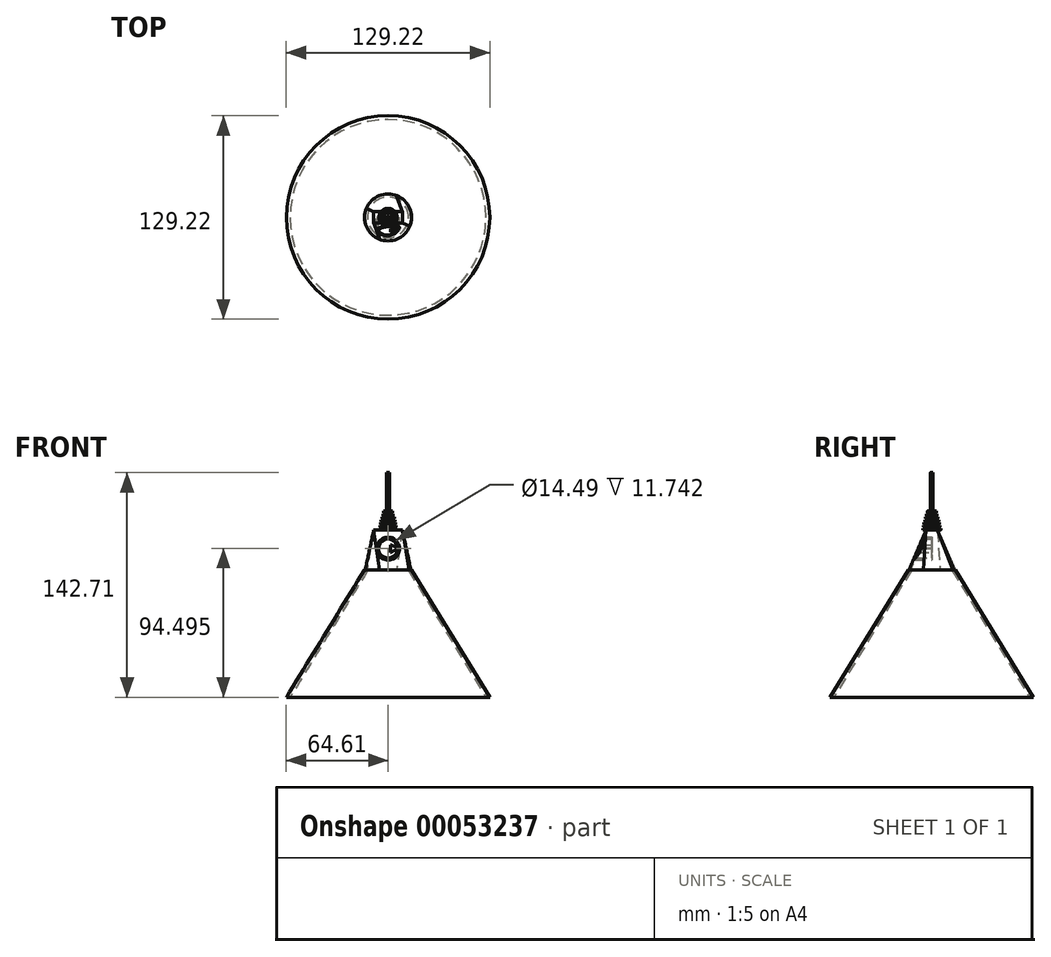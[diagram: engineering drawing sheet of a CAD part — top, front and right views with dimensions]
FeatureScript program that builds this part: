
annotation { "Feature Type Name" : "Feature", "Feature Type Description" : "" }
export const myFeature = defineFeature(function(context is Context, id is Id, definition is map)
    precondition{}
    {
        {
            var Q0;
            Q0=qCreatedBy(makeId("Top.planeOp"),FACE);
            var sketch = newSketch(context, id + "F0", { "sketchPlane" : qUnion([Q0])});
            skLineSegment(sketch, "E0.bottom", {"start": v(-9.08, 3.6) * mm, "end": v(9.08, 3.6) * mm});
            skLineSegment(sketch, "E0.top", {"start": v(-9.08, -3.6) * mm, "end": v(9.08, -3.6) * mm});
            skLineSegment(sketch, "E0.left", {"start": v(-9.08, 3.6) * mm, "end": v(-9.08, -3.6) * mm});
            skLineSegment(sketch, "E0.right", {"start": v(9.08, 3.6) * mm, "end": v(9.08, -3.6) * mm});
            skLineSegment(sketch, "E1", {"start": v(0, 3.6) * mm, "end": v(0, -3.6) * mm, "construction": true});
            skLineSegment(sketch, "E2", {"start": v(-9.08, 0) * mm, "end": v(9.08, 0) * mm, "construction": true});
            skSolve(sketch);
        }
        {
            var Q0;
            Q0=qCreatedBy(makeId("Top.planeOp"),FACE);
            cPlane(context, id + "F1", {"entities" : qUnion([Q0]), "cplaneType" : CPlaneType.OFFSET, "offset" : 25.4 * mm, "oppositeDirection" : true, "width" : 152.4 * mm, "height" : 152.4 * mm});
        }
        {
            var Q0;
            Q0=qCreatedBy(id+"F1.planeOp",FACE);
            var sketch = newSketch(context, id + "F2", { "sketchPlane" : qUnion([Q0])});
            skCircle(sketch, "E3", {"center": v(0, 0) * mm, "radius": 14.52 * mm});
            skSolve(sketch);
        }
        {
            var Q0;
            Q0=makeQuery(id+"F0.imprint","IMPRINT",FACE,{"disambiguationData":[TD([[makeQuery(id+"F0.imprint","IMPRINT",EDGE,{"derivedFrom":sQuery(id+"F0.wireOp",EDGE,"E0.bottom")}),-1.0]])]});
            var Q1;
            Q1=makeQuery(id+"F2.imprint","IMPRINT",FACE,{"disambiguationData":[TD([[makeQuery(id+"F2.imprint","IMPRINT",EDGE,{"derivedFrom":sQuery(id+"F2.wireOp",EDGE,"E3")}),1.0]])]});
            loft(context, id + "F3", {"sheetProfilesArray" : [{ "sheetProfileEntities" : qUnion([Q0]) }, { "sheetProfileEntities" : qUnion([Q1]) }]});
        }
        {
            var Q0;
            Q0=qCreatedBy(makeId("Front.planeOp"),FACE);
            var sketch = newSketch(context, id + "F4", { "sketchPlane" : qUnion([Q0])});
            skLineSegment(sketch, "E4", {"start": v(-14.94, -25.3) * mm, "end": v(-64.6, -106.22) * mm});
            skLineSegment(sketch, "E5", {"start": v(-64.6, -106.22) * mm, "end": v(-62.17, -106.22) * mm});
            skLineSegment(sketch, "E6", {"start": v(-62.17, -106.22) * mm, "end": v(-12.95, -25.52) * mm});
            skLineSegment(sketch, "E7", {"start": v(-12.95, -25.52) * mm, "end": v(-14.94, -25.3) * mm});
            skLineSegment(sketch, "E8", {"start": v(0, -122.63) * mm, "end": v(0, -14.43) * mm, "construction": true});
            skSolve(sketch);
        }
        {
            var Q0;
            Q0 = qSketchRegion(id + "F4", true);
            var Q1;
            Q1=sQuery(id+"F4.wireOp",EDGE,"E8");
            revolve(context, id + "F5", {"entities" : qUnion([Q0]), "axis" : qUnion([Q1]), "revolveType" : RevolveType.FULL});
        }
        {
            var Q0;
            Q0=qCreatedBy(makeId("Front.planeOp"),FACE);
            var sketch = newSketch(context, id + "F6", { "sketchPlane" : qUnion([Q0])});
            skLineSegment(sketch, "E9", {"start": v(0, 36.49) * mm, "end": v(0.88, 36.49) * mm});
            skLineSegment(sketch, "E10", {"start": v(0.88, 36.49) * mm, "end": v(0.88, 11.98) * mm});
            skLineSegment(sketch, "E11", {"start": v(0.88, 11.98) * mm, "end": v(2.84, 11.98) * mm});
            skLineSegment(sketch, "E12", {"start": v(2.84, 11.98) * mm, "end": v(2.84, 10.89) * mm});
            skLineSegment(sketch, "E13", {"start": v(2.84, 10.89) * mm, "end": v(0.88, 10.89) * mm});
            skLineSegment(sketch, "E14", {"start": v(0.88, 10.89) * mm, "end": v(0.88, 10.17) * mm});
            skLineSegment(sketch, "E15", {"start": v(0.88, 10.17) * mm, "end": v(3.29, 10.17) * mm});
            skLineSegment(sketch, "E16", {"start": v(3.29, 10.17) * mm, "end": v(3.29, 9.07) * mm});
            skLineSegment(sketch, "E17", {"start": v(3.29, 9.07) * mm, "end": v(0.88, 9.07) * mm});
            skLineSegment(sketch, "E18", {"start": v(0.88, 9.07) * mm, "end": v(0.88, 8.35) * mm});
            skLineSegment(sketch, "E19", {"start": v(0.88, 8.35) * mm, "end": v(3.96, 8.35) * mm});
            skLineSegment(sketch, "E20", {"start": v(3.96, 8.35) * mm, "end": v(3.96, 7.26) * mm});
            skLineSegment(sketch, "E21", {"start": v(3.96, 7.26) * mm, "end": v(0.88, 7.26) * mm});
            skLineSegment(sketch, "E22", {"start": v(0.88, 7.26) * mm, "end": v(0.88, 6.54) * mm});
            skLineSegment(sketch, "E23", {"start": v(0.88, 6.54) * mm, "end": v(4.5, 6.54) * mm});
            skLineSegment(sketch, "E24", {"start": v(4.5, 6.54) * mm, "end": v(4.5, 5.44) * mm});
            skLineSegment(sketch, "E25", {"start": v(4.5, 5.44) * mm, "end": v(0.88, 5.44) * mm});
            skLineSegment(sketch, "E26", {"start": v(0.88, 5.44) * mm, "end": v(0.88, 4.72) * mm});
            skLineSegment(sketch, "E27", {"start": v(0.88, 4.72) * mm, "end": v(4.88, 4.72) * mm});
            skLineSegment(sketch, "E28", {"start": v(4.88, 4.72) * mm, "end": v(4.88, 3.63) * mm});
            skLineSegment(sketch, "E29", {"start": v(4.88, 3.63) * mm, "end": v(0.88, 3.63) * mm});
            skLineSegment(sketch, "E30", {"start": v(0.88, 3.63) * mm, "end": v(0.88, 2.9) * mm});
            skLineSegment(sketch, "E31", {"start": v(0.88, 2.9) * mm, "end": v(5.21, 2.9) * mm});
            skLineSegment(sketch, "E32", {"start": v(5.21, 2.9) * mm, "end": v(5.21, 1.81) * mm});
            skLineSegment(sketch, "E33", {"start": v(5.21, 1.81) * mm, "end": v(0.88, 1.81) * mm});
            skLineSegment(sketch, "E34", {"start": v(0.88, 1.81) * mm, "end": v(0.88, 1.1) * mm});
            skLineSegment(sketch, "E35", {"start": v(0.88, 1.1) * mm, "end": v(5.7, 1.1) * mm});
            skLineSegment(sketch, "E36", {"start": v(5.7, 1.1) * mm, "end": v(5.7, 0) * mm});
            skLineSegment(sketch, "E37", {"start": v(5.7, 0) * mm, "end": v(0.88, 0) * mm});
            skLineSegment(sketch, "E38", {"start": v(0.88, 0) * mm, "end": v(0.88, -0.82) * mm});
            skLineSegment(sketch, "E39", {"start": v(0.88, -0.82) * mm, "end": v(2.9, -0.82) * mm});
            skLineSegment(sketch, "E40", {"start": v(2.9, -0.82) * mm, "end": v(1.12, -4.72) * mm});
            skLineSegment(sketch, "E41", {"start": v(1.12, -4.72) * mm, "end": v(0, -4.72) * mm});
            skLineSegment(sketch, "E42", {"start": v(0, -4.72) * mm, "end": v(0, 36.49) * mm});
            skLineSegment(sketch, "E43", {"start": v(0, 43.22) * mm, "end": v(0, 5.56) * mm, "construction": true});
            skSolve(sketch);
        }
        {
            var Q0;
            Q0 = qSketchRegion(id + "F6", true);
            var Q1;
            Q1=sQuery(id+"F6.wireOp",EDGE,"E43");
            revolve(context, id + "F7", {"operationType" : NewBodyOperationType.ADD, "entities" : qUnion([Q0]), "axis" : qUnion([Q1]), "revolveType" : RevolveType.FULL});
        }
        {
            var Q0;
            Q0=qCreatedBy(makeId("Front.planeOp"),FACE);
            var sketch = newSketch(context, id + "F8", { "sketchPlane" : qUnion([Q0])});
            skCircle(sketch, "E44", {"center": v(0, -11.72) * mm, "radius": 7.25 * mm});
            skArc(sketch, "E45", {"start": v(-6.04, -11.75) * mm, "mid": v(0, -17.77) * mm, "end": v(6.04, -11.75) * mm});
            skLineSegment(sketch, "E46", {"start": v(0, -1.4) * mm, "end": v(0, -21.08) * mm, "construction": true});
            skLineSegment(sketch, "E47.MirrorCS", {"start": v(1.72, -9.42) * mm, "end": v(1.72, -14.23) * mm});
            skLineSegment(sketch, "E48.MirrorCS", {"start": v(6.03, -11.27) * mm, "end": v(1.72, -9.42) * mm});
            skLineSegment(sketch, "E49.MirrorCS", {"start": v(1.72, -14.23) * mm, "end": v(6.04, -11.75) * mm});
            skArc(sketch, "E50.MirrorCS", {"start": v(6.04, -11.75) * mm, "mid": v(-6.04, -11.94) * mm, "end": v(6.03, -11.27) * mm});
            skArc(sketch, "E51.trimOffspring", {"start": v(6.03, -11.27) * mm, "mid": v(0, -5.68) * mm, "end": v(-6.03, -11.27) * mm});
            skSolve(sketch);
        }
        {
            var Q0;
            Q0 = qSketchRegion(id + "F8", true);
            extrude(context, id + "F9", {"entities" : qUnion([Q0]), "operationType" : NewBodyOperationType.REMOVE, "depth" : 12.7 * mm});
        }
    });
